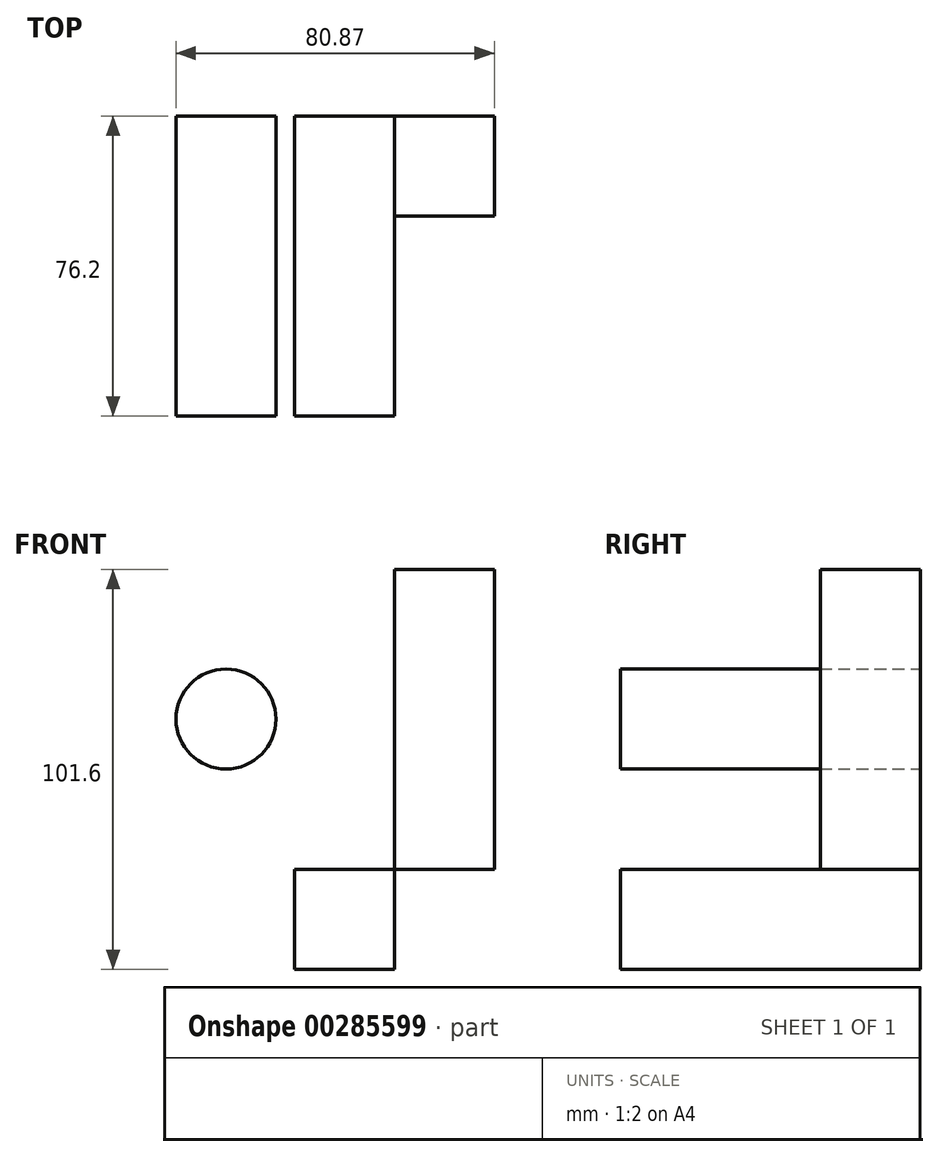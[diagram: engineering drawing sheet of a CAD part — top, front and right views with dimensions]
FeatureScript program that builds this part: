
annotation { "Feature Type Name" : "Feature", "Feature Type Description" : "" }
export const myFeature = defineFeature(function(context is Context, id is Id, definition is map)
    precondition{}
    {
        {
            var Q0;
            Q0=qCreatedBy(makeId("Front.planeOp"),FACE);
            var sketch = newSketch(context, id + "F0", { "sketchPlane" : qUnion([Q0])});
            skLineSegment(sketch, "E0.bottom", {"start": v(0, 0) * mm, "end": v(25.4, 0) * mm});
            skLineSegment(sketch, "E0.top", {"start": v(0, 76.2) * mm, "end": v(25.4, 76.2) * mm});
            skLineSegment(sketch, "E0.left", {"start": v(0, 0) * mm, "end": v(0, 76.2) * mm});
            skLineSegment(sketch, "E0.right", {"start": v(25.4, 0) * mm, "end": v(25.4, 76.2) * mm});
            skSolve(sketch);
        }
        {
            var Q0;
            Q0 = qSketchRegion(id + "F0", true);
            extrude(context, id + "F1", {"entities" : qUnion([Q0]), "depth" : 25.4 * mm});
        }
        {
            var Q0;
            Q0=qCreatedBy(makeId("Front.planeOp"),FACE);
            var sketch = newSketch(context, id + "F2", { "sketchPlane" : qUnion([Q0])});
            skCircle(sketch, "E1", {"center": v(-42.77, 38.2) * mm, "radius": 12.7 * mm});
            skSolve(sketch);
        }
        {
            var Q0;
            Q0 = qSketchRegion(id + "F2", true);
            extrude(context, id + "F3", {"entities" : qUnion([Q0]), "depth" : 76.2 * mm});
        }
        {
            var Q0;
            Q0=qCreatedBy(makeId("Front.planeOp"),FACE);
            var sketch = newSketch(context, id + "F4", { "sketchPlane" : qUnion([Q0])});
            skLineSegment(sketch, "E2.bottom", {"start": v(0, 0) * mm, "end": v(-25.4, 0) * mm});
            skLineSegment(sketch, "E2.top", {"start": v(0, -25.4) * mm, "end": v(-25.4, -25.4) * mm});
            skLineSegment(sketch, "E2.left", {"start": v(0, 0) * mm, "end": v(0, -25.4) * mm});
            skLineSegment(sketch, "E2.right", {"start": v(-25.4, 0) * mm, "end": v(-25.4, -25.4) * mm});
            skSolve(sketch);
        }
        {
            var Q0;
            Q0 = qSketchRegion(id + "F4", true);
            extrude(context, id + "F5", {"entities" : qUnion([Q0]), "depth" : 76.2 * mm});
        }
    });
